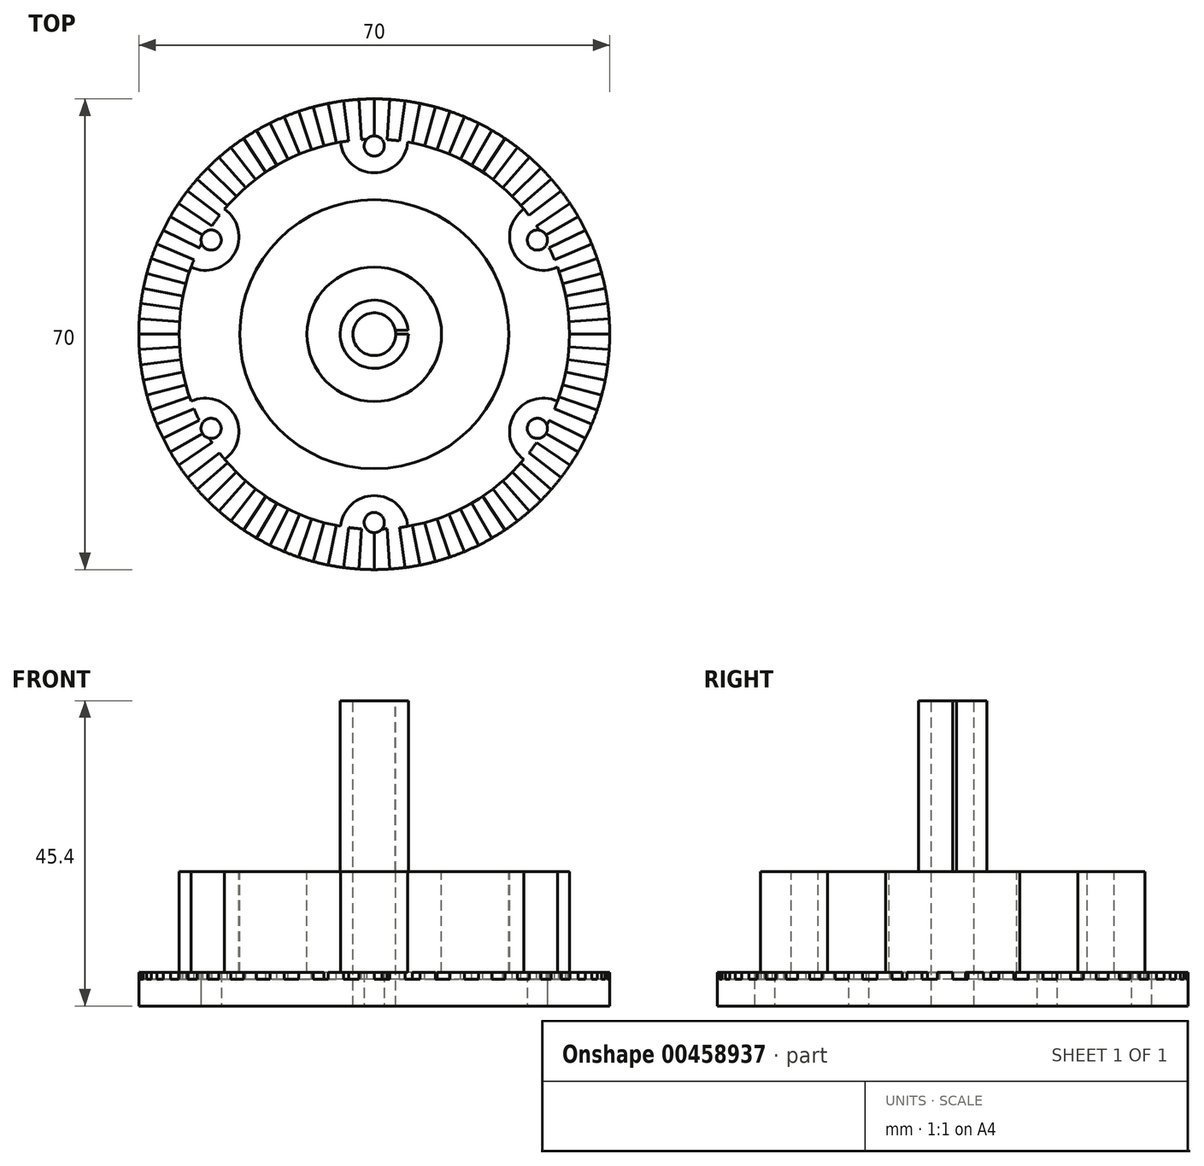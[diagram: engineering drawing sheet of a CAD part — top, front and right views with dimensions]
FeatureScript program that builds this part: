
annotation { "Feature Type Name" : "Feature", "Feature Type Description" : "" }
export const myFeature = defineFeature(function(context is Context, id is Id, definition is map)
    precondition{}
    {
        {
            var Q0;
            Q0=qCreatedBy(makeId("Top.planeOp"),FACE);
            var sketch = newSketch(context, id + "F0", { "sketchPlane" : qUnion([Q0])});
            skCircle(sketch, "E0", {"center": v(0, 0) * mm, "radius": 35 * mm});
            skSolve(sketch);
        }
        {
            var Q0;
            Q0=makeQuery(id+"F0.imprint","IMPRINT",FACE,{"disambiguationData":[TD([[makeQuery(id+"F0.imprint","IMPRINT",EDGE,{"derivedFrom":sQuery(id+"F0.wireOp",EDGE,"E0")}),1.0]])]});
            extrude(context, id + "F1", {"entities" : qUnion([Q0]), "depth" : 20 * mm});
        }
        {
            var Q0;
            Q0=makeQuery(id+"F1.opExtrude","CAP_FACE",FACE,{"disambiguationData":[OSD([sQuery(id+"F0.wireOp",EDGE,"E0")])],"isStart":false});
            var sketch = newSketch(context, id + "F2", { "sketchPlane" : qUnion([Q0])});
            skArc(sketch, "E1", {"start": v(4.98, -28.57) * mm, "mid": v(14.5, -25.11) * mm, "end": v(22.25, -18.6) * mm});
            skCircle(sketch, "E2", {"center": v(0, 0) * mm, "radius": 39.17 * mm});
            skLineSegment(sketch, "E3", {"start": v(0, 0) * mm, "end": v(0, -29) * mm, "construction": true});
            skArc(sketch, "E4", {"start": v(4.98, -28.57) * mm, "mid": v(0, -24) * mm, "end": v(-4.98, -28.57) * mm});
            skArc(sketch, "E5.trimOffspring", {"start": v(28.37, -6) * mm, "mid": v(28.93, 2.06) * mm, "end": v(27.23, 9.97) * mm});
            skArc(sketch, "E6.1.0", {"start": v(27.23, -9.97) * mm, "mid": v(20.78, -12) * mm, "end": v(22.25, -18.6) * mm});
            skArc(sketch, "E6.2.0", {"start": v(22.25, 18.6) * mm, "mid": v(20.78, 12) * mm, "end": v(27.23, 9.97) * mm});
            skArc(sketch, "E6.3.0", {"start": v(-4.98, 28.57) * mm, "mid": v(0, 24) * mm, "end": v(4.98, 28.57) * mm});
            skArc(sketch, "E6.4.0", {"start": v(-27.23, 9.97) * mm, "mid": v(-20.78, 12) * mm, "end": v(-22.25, 18.6) * mm});
            skArc(sketch, "E6.5.0", {"start": v(-22.25, -18.6) * mm, "mid": v(-20.78, -12) * mm, "end": v(-27.23, -9.97) * mm});
            skArc(sketch, "E7.trimOffspring", {"start": v(-22.25, -18.6) * mm, "mid": v(-14.5, -25.11) * mm, "end": v(-4.98, -28.57) * mm});
            skArc(sketch, "E8.trimOffspring", {"start": v(-27.23, 9.97) * mm, "mid": v(-29, 0) * mm, "end": v(-27.23, -9.97) * mm});
            skArc(sketch, "E9.trimOffspring", {"start": v(22.25, 18.6) * mm, "mid": v(14.5, 25.11) * mm, "end": v(4.98, 28.57) * mm});
            skArc(sketch, "E10.trimOffspring", {"start": v(27.23, -9.97) * mm, "mid": v(28.22, -6.66) * mm, "end": v(28.82, -3.26) * mm});
            skArc(sketch, "E11.trimOffspring", {"start": v(-4.98, 28.57) * mm, "mid": v(-14.5, 25.11) * mm, "end": v(-22.25, 18.6) * mm});
            skCircle(sketch, "E12", {"center": v(0, 0) * mm, "radius": 20 * mm});
            skCircle(sketch, "E13", {"center": v(0, 0) * mm, "radius": 10 * mm});
            skSolve(sketch);
        }
        {
            var Q0;
            Q0=makeQuery(id+"F2.imprint","IMPRINT",FACE,{"disambiguationData":[TD([[makeQuery(id+"F2.imprint","IMPRINT",EDGE,{"derivedFrom":sQuery(id+"F2.wireOp",EDGE,"E1")}),-1.0]])]});
            var Q1;
            Q1=makeQuery(id+"F2.imprint","IMPRINT",FACE,{"disambiguationData":[TD([[makeQuery(id+"F2.imprint","IMPRINT",EDGE,{"derivedFrom":sQuery(id+"F2.wireOp",EDGE,"E12")}),1.0]])]});
            extrude(context, id + "F3", {"entities" : qUnion([Q0, Q1]), "operationType" : NewBodyOperationType.REMOVE, "oppositeDirection" : true, "depth" : 15 * mm});
        }
        {
            var Q0;
            Q0=makeQuery(id+"F3.boolean.opBoolean","COPY",FACE,{"derivedFrom":makeQuery(id+"F3.opExtrude","CAP_FACE",FACE,{"disambiguationData":[OSD([sQuery(id+"F0.wireOp",EDGE,"E0"),sQuery(id+"F2.wireOp",EDGE,"E1"),sQuery(id+"F2.wireOp",EDGE,"E4"),sQuery(id+"F2.wireOp",EDGE,"a4c2945c-e413-476a-b8c3-20b808a95d02.1.0"),sQuery(id+"F2.wireOp",EDGE,"a4c2945c-e413-476a-b8c3-20b808a95d02.2.0"),sQuery(id+"F2.wireOp",EDGE,"a4c2945c-e413-476a-b8c3-20b808a95d02.3.0"),sQuery(id+"F2.wireOp",EDGE,"E5.trimOffspring"),sQuery(id+"F2.wireOp",EDGE,"ee2193d4-bcdd-46c0-b925-45254f04a156.trimOffspring"),sQuery(id+"F2.wireOp",EDGE,"514134c4-e0d3-45f8-a25c-7cd9b154419f.trimOffspring")])],"isStart":false})});
            var sketch = newSketch(context, id + "F4", { "sketchPlane" : qUnion([Q0])});
            skLineSegment(sketch, "E14", {"start": v(0, -35) * mm, "end": v(0, -29) * mm});
            skLineSegment(sketch, "E15", {"start": v(1.9, -28.94) * mm, "end": v(2.29, -34.93) * mm});
            skArc(sketch, "E16", {"start": v(2.29, -34.93) * mm, "mid": v(1.15, -34.98) * mm, "end": v(0, -35) * mm});
            skArc(sketch, "E17", {"start": v(1.9, -28.94) * mm, "mid": v(0.95, -28.98) * mm, "end": v(0, -29) * mm});
            skLineSegment(sketch, "E18.1.0", {"start": v(4.57, -34.7) * mm, "end": v(3.79, -28.75) * mm});
            skLineSegment(sketch, "E18.1.1", {"start": v(5.66, -28.44) * mm, "end": v(6.83, -34.33) * mm});
            skArc(sketch, "E18.1.2", {"start": v(5.66, -28.44) * mm, "mid": v(4.72, -28.61) * mm, "end": v(3.79, -28.75) * mm});
            skArc(sketch, "E18.1.3", {"start": v(6.83, -34.33) * mm, "mid": v(5.7, -34.53) * mm, "end": v(4.57, -34.7) * mm});
            skLineSegment(sketch, "E18.2.0", {"start": v(9.06, -33.8) * mm, "end": v(7.5, -28.01) * mm});
            skLineSegment(sketch, "E18.2.1", {"start": v(9.32, -27.46) * mm, "end": v(11.25, -33.14) * mm});
            skArc(sketch, "E18.2.2", {"start": v(9.32, -27.46) * mm, "mid": v(8.42, -27.75) * mm, "end": v(7.5, -28.01) * mm});
            skArc(sketch, "E18.2.3", {"start": v(11.25, -33.14) * mm, "mid": v(10.16, -33.5) * mm, "end": v(9.06, -33.8) * mm});
            skLineSegment(sketch, "E19.1.3.0", {"start": v(13.4, -32.34) * mm, "end": v(11.1, -26.8) * mm});
            skLineSegment(sketch, "E19.3.3.0", {"start": v(12.83, -26) * mm, "end": v(15.48, -31.4) * mm});
            skArc(sketch, "E19.6.3.0", {"start": v(12.83, -26) * mm, "mid": v(11.97, -26.42) * mm, "end": v(11.1, -26.8) * mm});
            skArc(sketch, "E19.10.3.0", {"start": v(15.48, -31.4) * mm, "mid": v(14.44, -31.88) * mm, "end": v(13.4, -32.34) * mm});
            skLineSegment(sketch, "E19.1.4.0", {"start": v(17.5, -30.31) * mm, "end": v(14.5, -25.11) * mm});
            skLineSegment(sketch, "E19.3.4.0", {"start": v(16.11, -24.11) * mm, "end": v(19.44, -29.1) * mm});
            skArc(sketch, "E19.6.4.0", {"start": v(16.11, -24.11) * mm, "mid": v(15.31, -24.63) * mm, "end": v(14.5, -25.11) * mm});
            skArc(sketch, "E19.10.4.0", {"start": v(19.44, -29.1) * mm, "mid": v(18.48, -29.72) * mm, "end": v(17.5, -30.31) * mm});
            skLineSegment(sketch, "E19.1.5.0", {"start": v(21.3, -27.77) * mm, "end": v(17.65, -23) * mm});
            skLineSegment(sketch, "E19.3.5.0", {"start": v(19.12, -21.8) * mm, "end": v(23.08, -26.31) * mm});
            skArc(sketch, "E19.6.5.0", {"start": v(19.12, -21.8) * mm, "mid": v(18.4, -22.42) * mm, "end": v(17.65, -23) * mm});
            skArc(sketch, "E19.10.5.0", {"start": v(23.08, -26.31) * mm, "mid": v(22.2, -27.06) * mm, "end": v(21.3, -27.77) * mm});
            skLineSegment(sketch, "E19.1.6.0", {"start": v(24.75, -24.75) * mm, "end": v(20.5, -20.5) * mm});
            skLineSegment(sketch, "E19.3.6.0", {"start": v(21.8, -19.12) * mm, "end": v(26.31, -23.08) * mm});
            skArc(sketch, "E19.6.6.0", {"start": v(21.8, -19.12) * mm, "mid": v(21.17, -19.82) * mm, "end": v(20.5, -20.5) * mm});
            skArc(sketch, "E19.10.6.0", {"start": v(26.31, -23.08) * mm, "mid": v(25.55, -23.93) * mm, "end": v(24.75, -24.75) * mm});
            skLineSegment(sketch, "E19.1.7.0", {"start": v(27.77, -21.3) * mm, "end": v(23, -17.65) * mm});
            skLineSegment(sketch, "E19.3.7.0", {"start": v(24.11, -16.11) * mm, "end": v(29.1, -19.44) * mm});
            skArc(sketch, "E19.6.7.0", {"start": v(24.11, -16.11) * mm, "mid": v(23.57, -16.9) * mm, "end": v(23, -17.65) * mm});
            skArc(sketch, "E19.10.7.0", {"start": v(29.1, -19.44) * mm, "mid": v(28.45, -20.39) * mm, "end": v(27.77, -21.3) * mm});
            skLineSegment(sketch, "E19.1.8.0", {"start": v(30.31, -17.5) * mm, "end": v(25.11, -14.5) * mm});
            skLineSegment(sketch, "E19.3.8.0", {"start": v(26, -12.83) * mm, "end": v(31.4, -15.48) * mm});
            skArc(sketch, "E19.6.8.0", {"start": v(26, -12.83) * mm, "mid": v(25.58, -13.67) * mm, "end": v(25.11, -14.5) * mm});
            skArc(sketch, "E19.10.8.0", {"start": v(31.4, -15.48) * mm, "mid": v(30.87, -16.5) * mm, "end": v(30.31, -17.5) * mm});
            skLineSegment(sketch, "E19.1.9.0", {"start": v(32.34, -13.4) * mm, "end": v(26.8, -11.1) * mm});
            skLineSegment(sketch, "E19.3.9.0", {"start": v(27.46, -9.32) * mm, "end": v(33.14, -11.25) * mm});
            skArc(sketch, "E19.6.9.0", {"start": v(27.46, -9.32) * mm, "mid": v(27.14, -10.22) * mm, "end": v(26.8, -11.1) * mm});
            skArc(sketch, "E19.10.9.0", {"start": v(33.14, -11.25) * mm, "mid": v(32.76, -12.33) * mm, "end": v(32.34, -13.4) * mm});
            skLineSegment(sketch, "E19.1.10.0", {"start": v(33.8, -9.06) * mm, "end": v(28.01, -7.5) * mm});
            skLineSegment(sketch, "E19.3.10.0", {"start": v(28.44, -5.66) * mm, "end": v(34.33, -6.83) * mm});
            skArc(sketch, "E19.6.10.0", {"start": v(28.44, -5.66) * mm, "mid": v(28.24, -6.59) * mm, "end": v(28.01, -7.5) * mm});
            skArc(sketch, "E19.10.10.0", {"start": v(34.33, -6.83) * mm, "mid": v(34.09, -7.95) * mm, "end": v(33.8, -9.06) * mm});
            skLineSegment(sketch, "E19.1.11.0", {"start": v(34.7, -4.57) * mm, "end": v(28.75, -3.79) * mm});
            skLineSegment(sketch, "E19.3.11.0", {"start": v(28.94, -1.9) * mm, "end": v(34.93, -2.29) * mm});
            skArc(sketch, "E19.6.11.0", {"start": v(28.94, -1.9) * mm, "mid": v(28.86, -2.84) * mm, "end": v(28.75, -3.79) * mm});
            skArc(sketch, "E19.10.11.0", {"start": v(34.93, -2.29) * mm, "mid": v(34.83, -3.43) * mm, "end": v(34.7, -4.57) * mm});
            skLineSegment(sketch, "E19.1.12.0", {"start": v(35, 0) * mm, "end": v(29, 0) * mm});
            skLineSegment(sketch, "E19.3.12.0", {"start": v(28.94, 1.9) * mm, "end": v(34.93, 2.29) * mm});
            skArc(sketch, "E19.6.12.0", {"start": v(28.94, 1.9) * mm, "mid": v(28.98, 0.95) * mm, "end": v(29, 0) * mm});
            skArc(sketch, "E19.10.12.0", {"start": v(34.93, 2.29) * mm, "mid": v(34.98, 1.15) * mm, "end": v(35, 0) * mm});
            skLineSegment(sketch, "E19.1.13.0", {"start": v(34.7, 4.57) * mm, "end": v(28.75, 3.79) * mm});
            skLineSegment(sketch, "E19.3.13.0", {"start": v(28.44, 5.66) * mm, "end": v(34.33, 6.83) * mm});
            skArc(sketch, "E19.6.13.0", {"start": v(28.44, 5.66) * mm, "mid": v(28.61, 4.72) * mm, "end": v(28.75, 3.79) * mm});
            skArc(sketch, "E19.10.13.0", {"start": v(34.33, 6.83) * mm, "mid": v(34.53, 5.7) * mm, "end": v(34.7, 4.57) * mm});
            skLineSegment(sketch, "E19.1.14.0", {"start": v(33.8, 9.06) * mm, "end": v(28.01, 7.5) * mm});
            skLineSegment(sketch, "E19.3.14.0", {"start": v(27.46, 9.32) * mm, "end": v(33.14, 11.25) * mm});
            skArc(sketch, "E19.6.14.0", {"start": v(27.46, 9.32) * mm, "mid": v(27.75, 8.42) * mm, "end": v(28.01, 7.5) * mm});
            skArc(sketch, "E19.10.14.0", {"start": v(33.14, 11.25) * mm, "mid": v(33.5, 10.16) * mm, "end": v(33.8, 9.06) * mm});
            skLineSegment(sketch, "E19.1.15.0", {"start": v(32.34, 13.4) * mm, "end": v(26.8, 11.1) * mm});
            skLineSegment(sketch, "E19.3.15.0", {"start": v(26, 12.83) * mm, "end": v(31.4, 15.48) * mm});
            skArc(sketch, "E19.6.15.0", {"start": v(26, 12.83) * mm, "mid": v(26.42, 11.97) * mm, "end": v(26.8, 11.1) * mm});
            skArc(sketch, "E19.10.15.0", {"start": v(31.4, 15.48) * mm, "mid": v(31.88, 14.44) * mm, "end": v(32.34, 13.4) * mm});
            skLineSegment(sketch, "E19.1.16.0", {"start": v(30.31, 17.5) * mm, "end": v(25.11, 14.5) * mm});
            skLineSegment(sketch, "E19.3.16.0", {"start": v(24.11, 16.11) * mm, "end": v(29.1, 19.44) * mm});
            skArc(sketch, "E19.6.16.0", {"start": v(24.11, 16.11) * mm, "mid": v(24.63, 15.31) * mm, "end": v(25.11, 14.5) * mm});
            skArc(sketch, "E19.10.16.0", {"start": v(29.1, 19.44) * mm, "mid": v(29.72, 18.48) * mm, "end": v(30.31, 17.5) * mm});
            skLineSegment(sketch, "E19.1.17.0", {"start": v(27.77, 21.3) * mm, "end": v(23, 17.65) * mm});
            skLineSegment(sketch, "E19.3.17.0", {"start": v(21.8, 19.12) * mm, "end": v(26.31, 23.08) * mm});
            skArc(sketch, "E19.6.17.0", {"start": v(21.8, 19.12) * mm, "mid": v(22.42, 18.4) * mm, "end": v(23, 17.65) * mm});
            skArc(sketch, "E19.10.17.0", {"start": v(26.31, 23.08) * mm, "mid": v(27.06, 22.2) * mm, "end": v(27.77, 21.3) * mm});
            skLineSegment(sketch, "E19.1.18.0", {"start": v(24.75, 24.75) * mm, "end": v(20.5, 20.5) * mm});
            skLineSegment(sketch, "E19.3.18.0", {"start": v(19.12, 21.8) * mm, "end": v(23.08, 26.31) * mm});
            skArc(sketch, "E19.6.18.0", {"start": v(19.12, 21.8) * mm, "mid": v(19.82, 21.17) * mm, "end": v(20.5, 20.5) * mm});
            skArc(sketch, "E19.10.18.0", {"start": v(23.08, 26.31) * mm, "mid": v(23.93, 25.55) * mm, "end": v(24.75, 24.75) * mm});
            skLineSegment(sketch, "E19.1.19.0", {"start": v(21.3, 27.77) * mm, "end": v(17.65, 23) * mm});
            skLineSegment(sketch, "E19.3.19.0", {"start": v(16.11, 24.11) * mm, "end": v(19.44, 29.1) * mm});
            skArc(sketch, "E19.6.19.0", {"start": v(16.11, 24.11) * mm, "mid": v(16.9, 23.57) * mm, "end": v(17.65, 23) * mm});
            skArc(sketch, "E19.10.19.0", {"start": v(19.44, 29.1) * mm, "mid": v(20.39, 28.45) * mm, "end": v(21.3, 27.77) * mm});
            skLineSegment(sketch, "E19.1.20.0", {"start": v(17.5, 30.31) * mm, "end": v(14.5, 25.11) * mm});
            skLineSegment(sketch, "E19.3.20.0", {"start": v(12.83, 26) * mm, "end": v(15.48, 31.4) * mm});
            skArc(sketch, "E19.6.20.0", {"start": v(12.83, 26) * mm, "mid": v(13.67, 25.58) * mm, "end": v(14.5, 25.11) * mm});
            skArc(sketch, "E19.10.20.0", {"start": v(15.48, 31.4) * mm, "mid": v(16.5, 30.87) * mm, "end": v(17.5, 30.31) * mm});
            skLineSegment(sketch, "E19.1.21.0", {"start": v(13.4, 32.34) * mm, "end": v(11.1, 26.8) * mm});
            skLineSegment(sketch, "E19.3.21.0", {"start": v(9.32, 27.46) * mm, "end": v(11.25, 33.14) * mm});
            skArc(sketch, "E19.6.21.0", {"start": v(9.32, 27.46) * mm, "mid": v(10.22, 27.14) * mm, "end": v(11.1, 26.8) * mm});
            skArc(sketch, "E19.10.21.0", {"start": v(11.25, 33.14) * mm, "mid": v(12.33, 32.76) * mm, "end": v(13.4, 32.34) * mm});
            skLineSegment(sketch, "E19.1.22.0", {"start": v(9.06, 33.8) * mm, "end": v(7.5, 28.01) * mm});
            skLineSegment(sketch, "E19.3.22.0", {"start": v(5.66, 28.44) * mm, "end": v(6.83, 34.33) * mm});
            skArc(sketch, "E19.6.22.0", {"start": v(5.66, 28.44) * mm, "mid": v(6.59, 28.24) * mm, "end": v(7.5, 28.01) * mm});
            skArc(sketch, "E19.10.22.0", {"start": v(6.83, 34.33) * mm, "mid": v(7.95, 34.09) * mm, "end": v(9.06, 33.8) * mm});
            skLineSegment(sketch, "E19.1.23.0", {"start": v(4.57, 34.7) * mm, "end": v(3.79, 28.75) * mm});
            skLineSegment(sketch, "E19.3.23.0", {"start": v(1.9, 28.94) * mm, "end": v(2.29, 34.93) * mm});
            skArc(sketch, "E19.6.23.0", {"start": v(1.9, 28.94) * mm, "mid": v(2.84, 28.86) * mm, "end": v(3.79, 28.75) * mm});
            skArc(sketch, "E19.10.23.0", {"start": v(2.29, 34.93) * mm, "mid": v(3.43, 34.83) * mm, "end": v(4.57, 34.7) * mm});
            skLineSegment(sketch, "E19.1.24.0", {"start": v(0, 35) * mm, "end": v(0, 29) * mm});
            skLineSegment(sketch, "E19.3.24.0", {"start": v(-1.9, 28.94) * mm, "end": v(-2.29, 34.93) * mm});
            skArc(sketch, "E19.6.24.0", {"start": v(-1.9, 28.94) * mm, "mid": v(-0.95, 28.98) * mm, "end": v(0, 29) * mm});
            skArc(sketch, "E19.10.24.0", {"start": v(-2.29, 34.93) * mm, "mid": v(-1.15, 34.98) * mm, "end": v(0, 35) * mm});
            skLineSegment(sketch, "E19.1.25.0", {"start": v(-4.57, 34.7) * mm, "end": v(-3.79, 28.75) * mm});
            skLineSegment(sketch, "E19.3.25.0", {"start": v(-5.66, 28.44) * mm, "end": v(-6.83, 34.33) * mm});
            skArc(sketch, "E19.6.25.0", {"start": v(-5.66, 28.44) * mm, "mid": v(-4.72, 28.61) * mm, "end": v(-3.79, 28.75) * mm});
            skArc(sketch, "E19.10.25.0", {"start": v(-6.83, 34.33) * mm, "mid": v(-5.7, 34.53) * mm, "end": v(-4.57, 34.7) * mm});
            skLineSegment(sketch, "E19.1.26.0", {"start": v(-9.06, 33.8) * mm, "end": v(-7.5, 28.01) * mm});
            skLineSegment(sketch, "E19.3.26.0", {"start": v(-9.32, 27.46) * mm, "end": v(-11.25, 33.14) * mm});
            skArc(sketch, "E19.6.26.0", {"start": v(-9.32, 27.46) * mm, "mid": v(-8.42, 27.75) * mm, "end": v(-7.5, 28.01) * mm});
            skArc(sketch, "E19.10.26.0", {"start": v(-11.25, 33.14) * mm, "mid": v(-10.16, 33.5) * mm, "end": v(-9.06, 33.8) * mm});
            skLineSegment(sketch, "E19.1.27.0", {"start": v(-13.4, 32.34) * mm, "end": v(-11.1, 26.8) * mm});
            skLineSegment(sketch, "E19.3.27.0", {"start": v(-12.83, 26) * mm, "end": v(-15.48, 31.4) * mm});
            skArc(sketch, "E19.6.27.0", {"start": v(-12.83, 26) * mm, "mid": v(-11.97, 26.42) * mm, "end": v(-11.1, 26.8) * mm});
            skArc(sketch, "E19.10.27.0", {"start": v(-15.48, 31.4) * mm, "mid": v(-14.44, 31.88) * mm, "end": v(-13.4, 32.34) * mm});
            skLineSegment(sketch, "E19.1.28.0", {"start": v(-17.5, 30.31) * mm, "end": v(-14.5, 25.11) * mm});
            skLineSegment(sketch, "E19.3.28.0", {"start": v(-16.11, 24.11) * mm, "end": v(-19.44, 29.1) * mm});
            skArc(sketch, "E19.6.28.0", {"start": v(-16.11, 24.11) * mm, "mid": v(-15.31, 24.63) * mm, "end": v(-14.5, 25.11) * mm});
            skArc(sketch, "E19.10.28.0", {"start": v(-19.44, 29.1) * mm, "mid": v(-18.48, 29.72) * mm, "end": v(-17.5, 30.31) * mm});
            skLineSegment(sketch, "E19.1.29.0", {"start": v(-21.3, 27.77) * mm, "end": v(-17.65, 23) * mm});
            skLineSegment(sketch, "E19.3.29.0", {"start": v(-19.12, 21.8) * mm, "end": v(-23.08, 26.31) * mm});
            skArc(sketch, "E19.6.29.0", {"start": v(-19.12, 21.8) * mm, "mid": v(-18.4, 22.42) * mm, "end": v(-17.65, 23) * mm});
            skArc(sketch, "E19.10.29.0", {"start": v(-23.08, 26.31) * mm, "mid": v(-22.2, 27.06) * mm, "end": v(-21.3, 27.77) * mm});
            skLineSegment(sketch, "E19.1.30.0", {"start": v(-24.75, 24.75) * mm, "end": v(-20.5, 20.5) * mm});
            skLineSegment(sketch, "E19.3.30.0", {"start": v(-21.8, 19.12) * mm, "end": v(-26.31, 23.08) * mm});
            skArc(sketch, "E19.6.30.0", {"start": v(-21.8, 19.12) * mm, "mid": v(-21.17, 19.82) * mm, "end": v(-20.5, 20.5) * mm});
            skArc(sketch, "E19.10.30.0", {"start": v(-26.31, 23.08) * mm, "mid": v(-25.55, 23.93) * mm, "end": v(-24.75, 24.75) * mm});
            skLineSegment(sketch, "E19.1.31.0", {"start": v(-27.77, 21.3) * mm, "end": v(-23, 17.65) * mm});
            skLineSegment(sketch, "E19.3.31.0", {"start": v(-24.11, 16.11) * mm, "end": v(-29.1, 19.44) * mm});
            skArc(sketch, "E19.6.31.0", {"start": v(-24.11, 16.11) * mm, "mid": v(-23.57, 16.9) * mm, "end": v(-23, 17.65) * mm});
            skArc(sketch, "E19.10.31.0", {"start": v(-29.1, 19.44) * mm, "mid": v(-28.45, 20.39) * mm, "end": v(-27.77, 21.3) * mm});
            skLineSegment(sketch, "E19.1.32.0", {"start": v(-30.31, 17.5) * mm, "end": v(-25.11, 14.5) * mm});
            skLineSegment(sketch, "E19.3.32.0", {"start": v(-26, 12.83) * mm, "end": v(-31.4, 15.48) * mm});
            skArc(sketch, "E19.6.32.0", {"start": v(-26, 12.83) * mm, "mid": v(-25.58, 13.67) * mm, "end": v(-25.11, 14.5) * mm});
            skArc(sketch, "E19.10.32.0", {"start": v(-31.4, 15.48) * mm, "mid": v(-30.87, 16.5) * mm, "end": v(-30.31, 17.5) * mm});
            skLineSegment(sketch, "E19.1.33.0", {"start": v(-32.34, 13.4) * mm, "end": v(-26.8, 11.1) * mm});
            skLineSegment(sketch, "E19.3.33.0", {"start": v(-27.46, 9.32) * mm, "end": v(-33.14, 11.25) * mm});
            skArc(sketch, "E19.6.33.0", {"start": v(-27.46, 9.32) * mm, "mid": v(-27.14, 10.22) * mm, "end": v(-26.8, 11.1) * mm});
            skArc(sketch, "E19.10.33.0", {"start": v(-33.14, 11.25) * mm, "mid": v(-32.76, 12.33) * mm, "end": v(-32.34, 13.4) * mm});
            skLineSegment(sketch, "E19.1.34.0", {"start": v(-33.8, 9.06) * mm, "end": v(-28.01, 7.5) * mm});
            skLineSegment(sketch, "E19.3.34.0", {"start": v(-28.44, 5.66) * mm, "end": v(-34.33, 6.83) * mm});
            skArc(sketch, "E19.6.34.0", {"start": v(-28.44, 5.66) * mm, "mid": v(-28.24, 6.59) * mm, "end": v(-28.01, 7.5) * mm});
            skArc(sketch, "E19.10.34.0", {"start": v(-34.33, 6.83) * mm, "mid": v(-34.09, 7.95) * mm, "end": v(-33.8, 9.06) * mm});
            skLineSegment(sketch, "E19.1.35.0", {"start": v(-34.7, 4.57) * mm, "end": v(-28.75, 3.79) * mm});
            skLineSegment(sketch, "E19.3.35.0", {"start": v(-28.94, 1.9) * mm, "end": v(-34.93, 2.29) * mm});
            skArc(sketch, "E19.6.35.0", {"start": v(-28.94, 1.9) * mm, "mid": v(-28.86, 2.84) * mm, "end": v(-28.75, 3.79) * mm});
            skArc(sketch, "E19.10.35.0", {"start": v(-34.93, 2.29) * mm, "mid": v(-34.83, 3.43) * mm, "end": v(-34.7, 4.57) * mm});
            skLineSegment(sketch, "E20.1.36.0", {"start": v(-35, 0) * mm, "end": v(-29, 0) * mm});
            skLineSegment(sketch, "E20.3.36.0", {"start": v(-28.94, -1.9) * mm, "end": v(-34.93, -2.29) * mm});
            skArc(sketch, "E20.6.36.0", {"start": v(-28.94, -1.9) * mm, "mid": v(-28.98, -0.95) * mm, "end": v(-29, 0) * mm});
            skArc(sketch, "E20.10.36.0", {"start": v(-34.93, -2.29) * mm, "mid": v(-34.98, -1.15) * mm, "end": v(-35, 0) * mm});
            skLineSegment(sketch, "E20.1.37.0", {"start": v(-34.7, -4.57) * mm, "end": v(-28.75, -3.79) * mm});
            skLineSegment(sketch, "E20.3.37.0", {"start": v(-28.44, -5.66) * mm, "end": v(-34.33, -6.83) * mm});
            skArc(sketch, "E20.6.37.0", {"start": v(-28.44, -5.66) * mm, "mid": v(-28.61, -4.72) * mm, "end": v(-28.75, -3.79) * mm});
            skArc(sketch, "E20.10.37.0", {"start": v(-34.33, -6.83) * mm, "mid": v(-34.53, -5.7) * mm, "end": v(-34.7, -4.57) * mm});
            skLineSegment(sketch, "E20.1.38.0", {"start": v(-33.8, -9.06) * mm, "end": v(-28.01, -7.5) * mm});
            skLineSegment(sketch, "E20.3.38.0", {"start": v(-27.46, -9.32) * mm, "end": v(-33.14, -11.25) * mm});
            skArc(sketch, "E20.6.38.0", {"start": v(-27.46, -9.32) * mm, "mid": v(-27.75, -8.42) * mm, "end": v(-28.01, -7.5) * mm});
            skArc(sketch, "E20.10.38.0", {"start": v(-33.14, -11.25) * mm, "mid": v(-33.5, -10.16) * mm, "end": v(-33.8, -9.06) * mm});
            skLineSegment(sketch, "E20.1.39.0", {"start": v(-32.34, -13.4) * mm, "end": v(-26.8, -11.1) * mm});
            skLineSegment(sketch, "E20.3.39.0", {"start": v(-26, -12.83) * mm, "end": v(-31.4, -15.48) * mm});
            skArc(sketch, "E20.6.39.0", {"start": v(-26, -12.83) * mm, "mid": v(-26.42, -11.97) * mm, "end": v(-26.8, -11.1) * mm});
            skArc(sketch, "E20.10.39.0", {"start": v(-31.4, -15.48) * mm, "mid": v(-31.88, -14.44) * mm, "end": v(-32.34, -13.4) * mm});
            skLineSegment(sketch, "E20.1.40.0", {"start": v(-30.31, -17.5) * mm, "end": v(-25.11, -14.5) * mm});
            skLineSegment(sketch, "E20.3.40.0", {"start": v(-24.11, -16.11) * mm, "end": v(-29.1, -19.44) * mm});
            skArc(sketch, "E20.6.40.0", {"start": v(-24.11, -16.11) * mm, "mid": v(-24.63, -15.31) * mm, "end": v(-25.11, -14.5) * mm});
            skArc(sketch, "E20.10.40.0", {"start": v(-29.1, -19.44) * mm, "mid": v(-29.72, -18.48) * mm, "end": v(-30.31, -17.5) * mm});
            skLineSegment(sketch, "E20.1.41.0", {"start": v(-27.77, -21.3) * mm, "end": v(-23, -17.65) * mm});
            skLineSegment(sketch, "E20.3.41.0", {"start": v(-21.8, -19.12) * mm, "end": v(-26.31, -23.08) * mm});
            skArc(sketch, "E20.6.41.0", {"start": v(-21.8, -19.12) * mm, "mid": v(-22.42, -18.4) * mm, "end": v(-23, -17.65) * mm});
            skArc(sketch, "E20.10.41.0", {"start": v(-26.31, -23.08) * mm, "mid": v(-27.06, -22.2) * mm, "end": v(-27.77, -21.3) * mm});
            skLineSegment(sketch, "E20.1.42.0", {"start": v(-24.75, -24.75) * mm, "end": v(-20.5, -20.5) * mm});
            skLineSegment(sketch, "E20.3.42.0", {"start": v(-19.12, -21.8) * mm, "end": v(-23.08, -26.31) * mm});
            skArc(sketch, "E20.6.42.0", {"start": v(-19.12, -21.8) * mm, "mid": v(-19.82, -21.17) * mm, "end": v(-20.5, -20.5) * mm});
            skArc(sketch, "E20.10.42.0", {"start": v(-23.08, -26.31) * mm, "mid": v(-23.93, -25.55) * mm, "end": v(-24.75, -24.75) * mm});
            skLineSegment(sketch, "E20.1.43.0", {"start": v(-21.3, -27.77) * mm, "end": v(-17.65, -23) * mm});
            skLineSegment(sketch, "E20.3.43.0", {"start": v(-16.11, -24.11) * mm, "end": v(-19.44, -29.1) * mm});
            skArc(sketch, "E20.6.43.0", {"start": v(-16.11, -24.11) * mm, "mid": v(-16.9, -23.57) * mm, "end": v(-17.65, -23) * mm});
            skArc(sketch, "E20.10.43.0", {"start": v(-19.44, -29.1) * mm, "mid": v(-20.39, -28.45) * mm, "end": v(-21.3, -27.77) * mm});
            skLineSegment(sketch, "E20.1.44.0", {"start": v(-17.5, -30.31) * mm, "end": v(-14.5, -25.11) * mm});
            skLineSegment(sketch, "E20.3.44.0", {"start": v(-12.83, -26) * mm, "end": v(-15.48, -31.4) * mm});
            skArc(sketch, "E20.6.44.0", {"start": v(-12.83, -26) * mm, "mid": v(-13.67, -25.58) * mm, "end": v(-14.5, -25.11) * mm});
            skArc(sketch, "E20.10.44.0", {"start": v(-15.48, -31.4) * mm, "mid": v(-16.5, -30.87) * mm, "end": v(-17.5, -30.31) * mm});
            skLineSegment(sketch, "E20.1.45.0", {"start": v(-13.4, -32.34) * mm, "end": v(-11.1, -26.8) * mm});
            skLineSegment(sketch, "E20.3.45.0", {"start": v(-9.32, -27.46) * mm, "end": v(-11.25, -33.14) * mm});
            skArc(sketch, "E20.6.45.0", {"start": v(-9.32, -27.46) * mm, "mid": v(-10.22, -27.14) * mm, "end": v(-11.1, -26.8) * mm});
            skArc(sketch, "E20.10.45.0", {"start": v(-11.25, -33.14) * mm, "mid": v(-12.33, -32.76) * mm, "end": v(-13.4, -32.34) * mm});
            skLineSegment(sketch, "E20.1.46.0", {"start": v(-9.06, -33.8) * mm, "end": v(-7.5, -28.01) * mm});
            skLineSegment(sketch, "E20.3.46.0", {"start": v(-5.66, -28.44) * mm, "end": v(-6.83, -34.33) * mm});
            skArc(sketch, "E20.6.46.0", {"start": v(-5.66, -28.44) * mm, "mid": v(-6.59, -28.24) * mm, "end": v(-7.5, -28.01) * mm});
            skArc(sketch, "E20.10.46.0", {"start": v(-6.83, -34.33) * mm, "mid": v(-7.95, -34.09) * mm, "end": v(-9.06, -33.8) * mm});
            skLineSegment(sketch, "E20.1.47.0", {"start": v(-4.57, -34.7) * mm, "end": v(-3.79, -28.75) * mm});
            skLineSegment(sketch, "E20.3.47.0", {"start": v(-1.9, -28.94) * mm, "end": v(-2.29, -34.93) * mm});
            skArc(sketch, "E20.6.47.0", {"start": v(-1.9, -28.94) * mm, "mid": v(-2.84, -28.86) * mm, "end": v(-3.79, -28.75) * mm});
            skArc(sketch, "E20.10.47.0", {"start": v(-2.29, -34.93) * mm, "mid": v(-3.43, -34.83) * mm, "end": v(-4.57, -34.7) * mm});
            skSolve(sketch);
        }
        {
            var Q0;
            Q0=qSketchRegion(id+"F4",true);
            extrude(context, id + "F5", {"entities" : qUnion([Q0]), "operationType" : NewBodyOperationType.REMOVE, "oppositeDirection" : true, "depth" : 1 * mm});
        }
        {
            var Q0;
            Q0=makeQuery(id+"F1.opExtrude","CAP_FACE",FACE,{"disambiguationData":[OSD([sQuery(id+"F0.wireOp",EDGE,"E0")])],"isStart":false});
            var sketch = newSketch(context, id + "F6", { "sketchPlane" : qUnion([Q0])});
            skCircle(sketch, "E21", {"center": v(0, 0) * mm, "radius": 5.07 * mm});
            skSolve(sketch);
        }
        {
            var Q0;
            Q0=makeQuery(id+"F6.imprint","IMPRINT",FACE,{"disambiguationData":[TD([[makeQuery(id+"F6.imprint","IMPRINT",EDGE,{"derivedFrom":sQuery(id+"F6.wireOp",EDGE,"E21")}),1.0]])]});
            extrude(context, id + "F7", {"entities" : qUnion([Q0]), "operationType" : NewBodyOperationType.ADD, "depth" : 25.4 * mm});
        }
        {
            var Q0;
            Q0=makeQuery(id+"F7.opExtrude","CAP_FACE",FACE,{"disambiguationData":[OSD([sQuery(id+"F6.wireOp",EDGE,"E21")])],"isStart":false});
            var sketch = newSketch(context, id + "F8", { "sketchPlane" : qUnion([Q0])});
            skCircle(sketch, "E22", {"center": v(0, 0) * mm, "radius": 3.18 * mm});
            skSolve(sketch);
        }
        {
            var Q0;
            Q0=makeQuery(id+"F8.imprint","IMPRINT",FACE,{"disambiguationData":[TD([[makeQuery(id+"F8.imprint","IMPRINT",EDGE,{"derivedFrom":sQuery(id+"F8.wireOp",EDGE,"E22")}),1.0]])]});
            extrude(context, id + "F9", {"entities" : qUnion([Q0]), "operationType" : NewBodyOperationType.REMOVE, "endBound" : BoundingType.THROUGH_ALL, "oppositeDirection" : true, "depth" : 25.4 * mm});
        }
        {
            var Q0;
            Q0=makeQuery(id+"F7.opExtrude","CAP_FACE",FACE,{"disambiguationData":[OSD([sQuery(id+"F6.wireOp",EDGE,"E21")])],"isStart":false});
            var sketch = newSketch(context, id + "F10", { "sketchPlane" : qUnion([Q0])});
            skLineSegment(sketch, "E23.bottom", {"start": v(0, 0) * mm, "end": v(9.94, 0) * mm});
            skLineSegment(sketch, "E23.top", {"start": v(0, 0.58) * mm, "end": v(9.94, 0.58) * mm});
            skLineSegment(sketch, "E23.left", {"start": v(0, 0) * mm, "end": v(0, 0.58) * mm});
            skLineSegment(sketch, "E23.right", {"start": v(9.94, 0) * mm, "end": v(9.94, 0.58) * mm});
            skSolve(sketch);
        }
        {
            var Q0;
            {var subQ0=sQuery(id+"F10.wireOp",EDGE,"E23.bottom");var subQ1=makeQuery(id+"F7.opExtrude","CAP_EDGE",EDGE,{"disambiguationData":[OSD([sQuery(id+"F6.wireOp",EDGE,"E21")])],"isStart":false});var subQ2=makeQuery(id+"F10.imprint","INTERSECT",VERTEX,{"derivedFrom":[subQ1,subQ0]});Q0=makeQuery(id+"F10.imprint","IMPRINT",FACE,{"disambiguationData":[TD([[makeQuery(id+"F10.imprint","IMPRINT",EDGE,{"disambiguationData":[TD([[subQ2,1.0]])],"derivedFrom":subQ0}),1.0]])]});}
            var Q1;
            Q1=makeQuery(id+"F1.opExtrude","CAP_FACE",FACE,{"disambiguationData":[OSD([sQuery(id+"F0.wireOp",EDGE,"E0")])],"isStart":false});
            extrude(context, id + "F11", {"entities" : qUnion([Q0]), "operationType" : NewBodyOperationType.REMOVE, "endBound" : BoundingType.UP_TO_SURFACE, "oppositeDirection" : true, "endBoundEntityFace" : qUnion([Q1]), "depth" : 25.4 * mm});
        }
        {
            var Q0;
            Q0=makeQuery(id+"F0.imprint","IMPRINT",FACE,{"disambiguationData":[TD([[makeQuery(id+"F0.imprint","IMPRINT",EDGE,{"derivedFrom":sQuery(id+"F0.wireOp",EDGE,"E0")}),1.0]])]});
            var sketch = newSketch(context, id + "F12", { "sketchPlane" : qUnion([Q0])});
            skLineSegment(sketch, "E24", {"start": v(0, 0) * mm, "end": v(0, -16.9) * mm, "construction": true});
            skCircle(sketch, "E25", {"center": v(0, -28) * mm, "radius": 1.5 * mm});
            skCircle(sketch, "E26.1.0", {"center": v(24.25, -14) * mm, "radius": 1.5 * mm});
            skCircle(sketch, "E26.2.0", {"center": v(24.25, 14) * mm, "radius": 1.5 * mm});
            skCircle(sketch, "E26.3.0", {"center": v(0, 28) * mm, "radius": 1.5 * mm});
            skCircle(sketch, "E26.4.0", {"center": v(-24.25, 14) * mm, "radius": 1.5 * mm});
            skCircle(sketch, "E26.5.0", {"center": v(-24.25, -14) * mm, "radius": 1.5 * mm});
            skPoint(sketch, "E26.center", {"position": v(0, 0) * mm});
            skSolve(sketch);
        }
        {
            var Q0;
            Q0=qSketchRegion(id+"F12",true);
            extrude(context, id + "F13", {"entities" : qUnion([Q0]), "operationType" : NewBodyOperationType.REMOVE, "endBound" : BoundingType.THROUGH_ALL, "depth" : 25.4 * mm});
        }
    });
